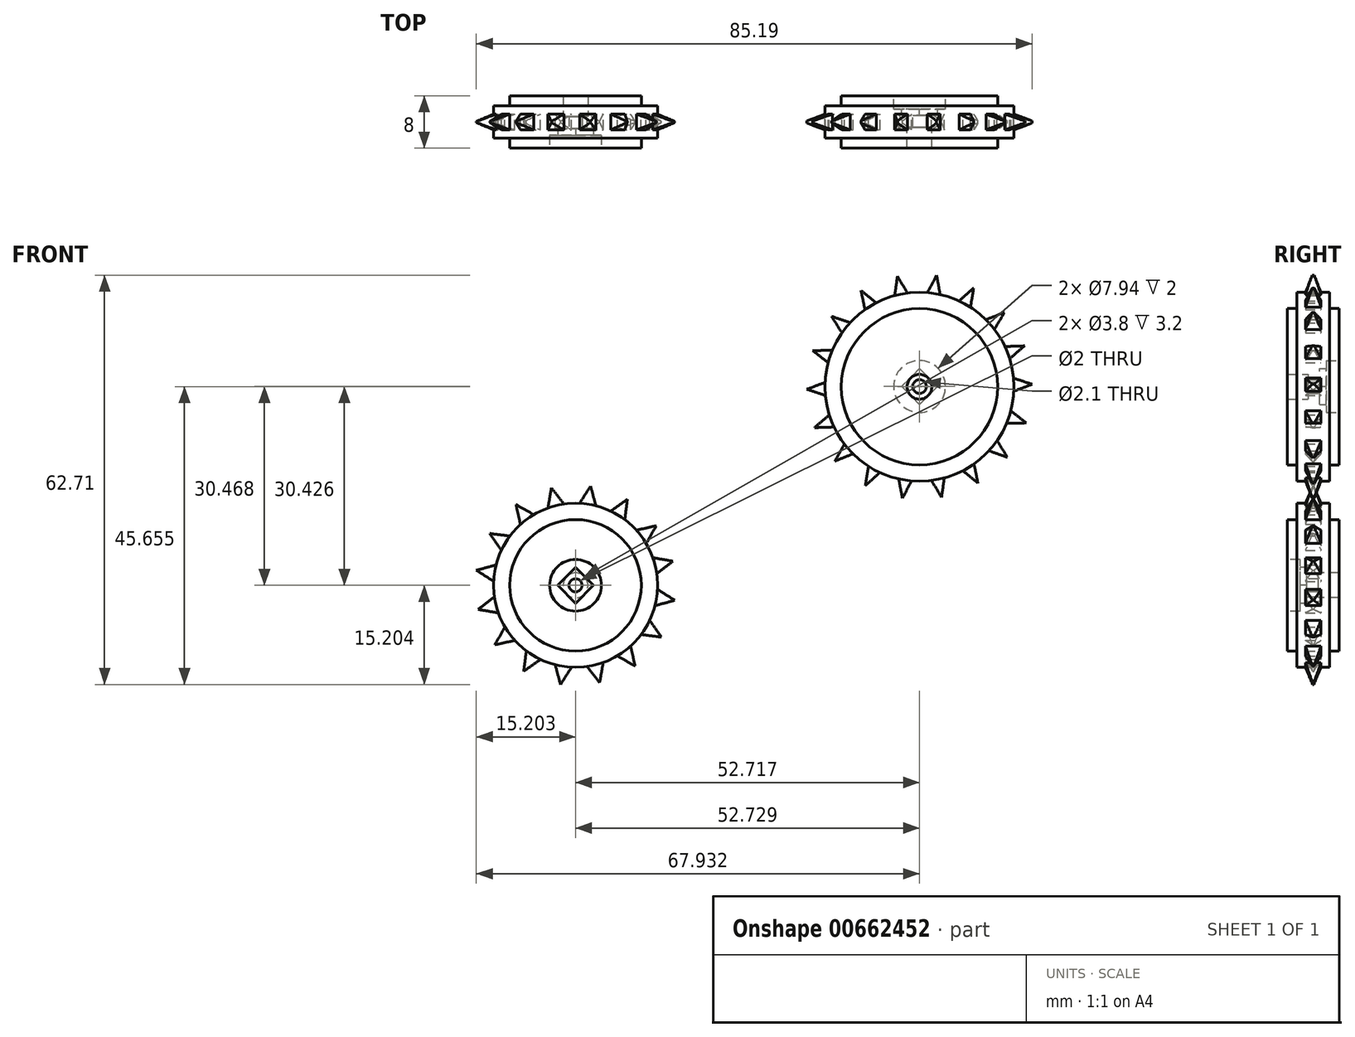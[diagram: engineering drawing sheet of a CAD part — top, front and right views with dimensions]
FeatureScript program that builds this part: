
annotation { "Feature Type Name" : "Feature", "Feature Type Description" : "" }
export const myFeature = defineFeature(function(context is Context, id is Id, definition is map)
    precondition{}
    {
        {
            var Q0;
            Q0=qCreatedBy(makeId("Front.planeOp"),FACE);
            var sketch = newSketch(context, id + "F0", { "sketchPlane" : qUnion([Q0])});
            skCircle(sketch, "E0.cCircle", {"center": v(0, 0) * mm, "radius": 17.01 * mm, "construction": true});
            skLineSegment(sketch, "E0.0", {"start": v(16.36, -5.55) * mm, "end": v(13.48, -10.8) * mm});
            skLineSegment(sketch, "E0.1", {"start": v(13.48, -10.8) * mm, "end": v(8.97, -14.77) * mm});
            skLineSegment(sketch, "E0.2", {"start": v(8.97, -14.77) * mm, "end": v(3.38, -16.94) * mm});
            skLineSegment(sketch, "E0.3", {"start": v(3.38, -16.94) * mm, "end": v(-2.62, -17.08) * mm});
            skLineSegment(sketch, "E0.4", {"start": v(-2.62, -17.08) * mm, "end": v(-8.3, -15.15) * mm});
            skLineSegment(sketch, "E0.5", {"start": v(-8.3, -15.15) * mm, "end": v(-12.98, -11.4) * mm});
            skLineSegment(sketch, "E0.6", {"start": v(-12.98, -11.4) * mm, "end": v(-16.1, -6.27) * mm});
            skLineSegment(sketch, "E0.7", {"start": v(-16.1, -6.27) * mm, "end": v(-17.27, -0.38) * mm});
            skLineSegment(sketch, "E0.8", {"start": v(-17.27, -0.38) * mm, "end": v(-16.36, 5.55) * mm});
            skLineSegment(sketch, "E0.9", {"start": v(-16.36, 5.55) * mm, "end": v(-13.48, 10.8) * mm});
            skLineSegment(sketch, "E0.10", {"start": v(-13.48, 10.8) * mm, "end": v(-8.97, 14.77) * mm});
            skLineSegment(sketch, "E0.11", {"start": v(-8.97, 14.77) * mm, "end": v(-3.38, 16.94) * mm});
            skLineSegment(sketch, "E0.12", {"start": v(-3.38, 16.94) * mm, "end": v(2.62, 17.08) * mm});
            skLineSegment(sketch, "E0.13", {"start": v(2.62, 17.08) * mm, "end": v(8.3, 15.15) * mm});
            skLineSegment(sketch, "E0.14", {"start": v(8.3, 15.15) * mm, "end": v(12.98, 11.4) * mm});
            skLineSegment(sketch, "E0.15", {"start": v(12.98, 11.4) * mm, "end": v(16.1, 6.27) * mm});
            skLineSegment(sketch, "E0.16", {"start": v(16.1, 6.27) * mm, "end": v(17.27, 0.38) * mm});
            skLineSegment(sketch, "E0.17", {"start": v(17.27, 0.38) * mm, "end": v(16.36, -5.55) * mm});
            skPoint(sketch, "E0.0.midPoint", {"position": v(14.92, -8.18) * mm});
            skLineSegment(sketch, "E1", {"start": v(-61.38, -2.75) * mm, "end": v(-43.67, -5.95) * mm});
            skLineSegment(sketch, "E2", {"start": v(-3.38, 16.94) * mm, "end": v(-2.83, 14.2) * mm, "construction": true});
            skLineSegment(sketch, "E3", {"start": v(-2.83, 14.2) * mm, "end": v(-2.34, 11.75) * mm, "construction": true});
            skLineSegment(sketch, "E4", {"start": v(-2.34, 11.75) * mm, "end": v(0, 0) * mm, "construction": true});
            skCircle(sketch, "E5", {"center": v(0, 0) * mm, "radius": 11.98 * mm});
            skCircle(sketch, "E6", {"center": v(0, 0) * mm, "radius": 14.48 * mm});
            skLineSegment(sketch, "E7", {"start": v(0, 0) * mm, "end": v(2.62, 17.08) * mm, "construction": true});
            skPoint(sketch, "E8", {"position": v(2.13, 13.85) * mm});
            skLineSegment(sketch, "E9", {"start": v(2.13, 13.85) * mm, "end": v(0.99, 14.03) * mm, "construction": true});
            skLineSegment(sketch, "E10", {"start": v(2.62, 17.08) * mm, "end": v(0.99, 14.03) * mm});
            skLineSegment(sketch, "E11.MirrorCS", {"start": v(2.62, 17.08) * mm, "end": v(3.26, 13.68) * mm});
            skLineSegment(sketch, "E12.14.0", {"start": v(16.7, 0.37) * mm, "end": v(13.41, 1.45) * mm});
            skPoint(sketch, "E13.0", {"position": v(0.01, 0.03) * mm});
            skCircle(sketch, "E14.cCircle", {"center": v(0.01, 0.03) * mm, "radius": 2.75 * mm, "construction": true});
            skLineSegment(sketch, "E14.0", {"start": v(-2.74, 0.03) * mm, "end": v(0.01, 2.78) * mm});
            skLineSegment(sketch, "E14.1", {"start": v(0.01, 2.78) * mm, "end": v(2.76, 0.03) * mm});
            skLineSegment(sketch, "E14.2", {"start": v(2.76, 0.03) * mm, "end": v(0.01, -2.73) * mm});
            skLineSegment(sketch, "E14.3", {"start": v(0.01, -2.73) * mm, "end": v(-2.74, 0.03) * mm});
            skCircle(sketch, "E15", {"center": v(0.01, 0.03) * mm, "radius": 1.05 * mm});
            skCircle(sketch, "E16", {"center": v(0.01, 0.03) * mm, "radius": 3.97 * mm});
            skLineSegment(sketch, "E17", {"start": v(2.13, 13.85) * mm, "end": v(2.75, 17.9) * mm});
            skLineSegment(sketch, "E18.1.0", {"start": v(-2.74, 13.75) * mm, "end": v(-3.87, 13.52) * mm, "construction": true});
            skPoint(sketch, "E18.1.1", {"position": v(-2.74, 13.75) * mm});
            skLineSegment(sketch, "E18.1.2", {"start": v(-3.38, 16.94) * mm, "end": v(-3.87, 13.52) * mm});
            skLineSegment(sketch, "E18.1.3", {"start": v(-3.38, 16.94) * mm, "end": v(-1.61, 13.97) * mm});
            skLineSegment(sketch, "E18.2.0", {"start": v(-7.28, 11.98) * mm, "end": v(-8.26, 11.38) * mm, "construction": true});
            skPoint(sketch, "E18.2.1", {"position": v(-7.28, 11.98) * mm});
            skLineSegment(sketch, "E18.2.2", {"start": v(-8.97, 14.77) * mm, "end": v(-8.26, 11.38) * mm});
            skLineSegment(sketch, "E18.2.3", {"start": v(-8.97, 14.77) * mm, "end": v(-6.3, 12.58) * mm});
            skLineSegment(sketch, "E18.3.0", {"start": v(-10.94, 8.77) * mm, "end": v(-11.66, 7.87) * mm, "construction": true});
            skPoint(sketch, "E18.3.1", {"position": v(-10.94, 8.77) * mm});
            skLineSegment(sketch, "E18.3.2", {"start": v(-13.48, 10.8) * mm, "end": v(-11.66, 7.87) * mm});
            skLineSegment(sketch, "E18.3.3", {"start": v(-13.48, 10.8) * mm, "end": v(-10.22, 9.67) * mm});
            skLineSegment(sketch, "E18.4.0", {"start": v(-13.28, 4.5) * mm, "end": v(-13.64, 3.41) * mm, "construction": true});
            skPoint(sketch, "E18.4.1", {"position": v(-13.28, 4.5) * mm});
            skLineSegment(sketch, "E18.4.2", {"start": v(-16.36, 5.55) * mm, "end": v(-13.64, 3.41) * mm});
            skLineSegment(sketch, "E18.4.3", {"start": v(-16.36, 5.55) * mm, "end": v(-12.9, 5.59) * mm});
            skLineSegment(sketch, "E18.5.0", {"start": v(-14.01, -0.31) * mm, "end": v(-13.99, -1.46) * mm, "construction": true});
            skPoint(sketch, "E18.5.1", {"position": v(-14.01, -0.31) * mm});
            skLineSegment(sketch, "E18.5.2", {"start": v(-17.27, -0.38) * mm, "end": v(-13.99, -1.46) * mm});
            skLineSegment(sketch, "E18.5.3", {"start": v(-17.27, -0.38) * mm, "end": v(-14.04, 0.84) * mm});
            skLineSegment(sketch, "E18.6.0", {"start": v(-13.06, -5.09) * mm, "end": v(-12.64, -6.16) * mm, "construction": true});
            skPoint(sketch, "E18.6.1", {"position": v(-13.06, -5.09) * mm});
            skLineSegment(sketch, "E18.6.2", {"start": v(-16.1, -6.27) * mm, "end": v(-12.64, -6.16) * mm});
            skLineSegment(sketch, "E18.6.3", {"start": v(-16.1, -6.27) * mm, "end": v(-13.48, -4.01) * mm});
            skLineSegment(sketch, "E18.7.0", {"start": v(-10.53, -9.25) * mm, "end": v(-9.78, -10.11) * mm, "construction": true});
            skPoint(sketch, "E18.7.1", {"position": v(-10.53, -9.25) * mm});
            skLineSegment(sketch, "E18.7.2", {"start": v(-12.98, -11.4) * mm, "end": v(-9.78, -10.11) * mm});
            skLineSegment(sketch, "E18.7.3", {"start": v(-12.98, -11.4) * mm, "end": v(-11.3, -8.38) * mm});
            skLineSegment(sketch, "E18.8.0", {"start": v(-6.74, -12.3) * mm, "end": v(-5.73, -12.84) * mm, "construction": true});
            skPoint(sketch, "E18.8.1", {"position": v(-6.74, -12.3) * mm});
            skLineSegment(sketch, "E18.8.2", {"start": v(-8.3, -15.15) * mm, "end": v(-5.73, -12.84) * mm});
            skLineSegment(sketch, "E18.8.3", {"start": v(-8.3, -15.15) * mm, "end": v(-7.75, -11.74) * mm});
            skLineSegment(sketch, "E18.9.0", {"start": v(-2.13, -13.85) * mm, "end": v(-0.99, -14.03) * mm, "construction": true});
            skPoint(sketch, "E18.9.1", {"position": v(-2.13, -13.85) * mm});
            skLineSegment(sketch, "E18.9.2", {"start": v(-2.62, -17.08) * mm, "end": v(-0.99, -14.03) * mm});
            skLineSegment(sketch, "E18.9.3", {"start": v(-2.62, -17.08) * mm, "end": v(-3.26, -13.68) * mm});
            skLineSegment(sketch, "E18.10.0", {"start": v(2.74, -13.75) * mm, "end": v(3.87, -13.52) * mm, "construction": true});
            skPoint(sketch, "E18.10.1", {"position": v(2.74, -13.75) * mm});
            skLineSegment(sketch, "E18.10.2", {"start": v(3.38, -16.94) * mm, "end": v(3.87, -13.52) * mm});
            skLineSegment(sketch, "E18.10.3", {"start": v(3.38, -16.94) * mm, "end": v(1.61, -13.97) * mm});
            skLineSegment(sketch, "E18.11.0", {"start": v(7.28, -11.98) * mm, "end": v(8.26, -11.38) * mm, "construction": true});
            skPoint(sketch, "E18.11.1", {"position": v(7.28, -11.98) * mm});
            skLineSegment(sketch, "E18.11.2", {"start": v(8.97, -14.77) * mm, "end": v(8.26, -11.38) * mm});
            skLineSegment(sketch, "E18.11.3", {"start": v(8.97, -14.77) * mm, "end": v(6.3, -12.58) * mm});
            skLineSegment(sketch, "E18.12.0", {"start": v(10.94, -8.77) * mm, "end": v(11.66, -7.87) * mm, "construction": true});
            skPoint(sketch, "E18.12.1", {"position": v(10.94, -8.77) * mm});
            skLineSegment(sketch, "E18.12.2", {"start": v(13.48, -10.8) * mm, "end": v(11.66, -7.87) * mm});
            skLineSegment(sketch, "E18.12.3", {"start": v(13.48, -10.8) * mm, "end": v(10.22, -9.67) * mm});
            skLineSegment(sketch, "E18.13.0", {"start": v(13.28, -4.5) * mm, "end": v(13.64, -3.41) * mm, "construction": true});
            skPoint(sketch, "E18.13.1", {"position": v(13.28, -4.5) * mm});
            skLineSegment(sketch, "E18.13.2", {"start": v(16.36, -5.55) * mm, "end": v(13.64, -3.41) * mm});
            skLineSegment(sketch, "E18.13.3", {"start": v(16.36, -5.55) * mm, "end": v(12.9, -5.59) * mm});
            skLineSegment(sketch, "E18.14.0", {"start": v(14.01, 0.31) * mm, "end": v(13.99, 1.46) * mm, "construction": true});
            skPoint(sketch, "E18.14.1", {"position": v(14.01, 0.31) * mm});
            skLineSegment(sketch, "E18.14.2", {"start": v(17.27, 0.38) * mm, "end": v(13.99, 1.46) * mm});
            skLineSegment(sketch, "E18.14.3", {"start": v(17.27, 0.38) * mm, "end": v(14.04, -0.84) * mm});
            skLineSegment(sketch, "E18.15.0", {"start": v(13.06, 5.09) * mm, "end": v(12.64, 6.16) * mm, "construction": true});
            skPoint(sketch, "E18.15.1", {"position": v(13.06, 5.09) * mm});
            skLineSegment(sketch, "E18.15.2", {"start": v(16.1, 6.27) * mm, "end": v(12.64, 6.16) * mm});
            skLineSegment(sketch, "E18.15.3", {"start": v(16.1, 6.27) * mm, "end": v(13.48, 4.01) * mm});
            skLineSegment(sketch, "E18.16.0", {"start": v(10.53, 9.25) * mm, "end": v(9.78, 10.11) * mm, "construction": true});
            skPoint(sketch, "E18.16.1", {"position": v(10.53, 9.25) * mm});
            skLineSegment(sketch, "E18.16.2", {"start": v(12.98, 11.4) * mm, "end": v(9.78, 10.11) * mm});
            skLineSegment(sketch, "E18.16.3", {"start": v(12.98, 11.4) * mm, "end": v(11.3, 8.38) * mm});
            skLineSegment(sketch, "E18.17.0", {"start": v(6.74, 12.3) * mm, "end": v(5.73, 12.84) * mm, "construction": true});
            skPoint(sketch, "E18.17.1", {"position": v(6.74, 12.3) * mm});
            skLineSegment(sketch, "E18.17.2", {"start": v(8.3, 15.15) * mm, "end": v(5.73, 12.84) * mm});
            skLineSegment(sketch, "E18.17.3", {"start": v(8.3, 15.15) * mm, "end": v(7.75, 11.74) * mm});
            skSolve(sketch);
        }
        {
            var Q0;
            Q0=makeQuery(id+"F0.imprint","IMPRINT",FACE,{"disambiguationData":[TD([[makeQuery(id+"F0.imprint","IMPRINT",EDGE,{"derivedFrom":sQuery(id+"F0.wireOp",EDGE,"E5")}),-1.0]])]});
            var Q1;
            {var subQ0=sQuery(id+"F0.wireOp",EDGE,"E12.7.1");var subQ1=sQuery(id+"F0.wireOp",EDGE,"E6");var subQ2=makeQuery(id+"F0.imprint","INTERSECT",VERTEX,{"derivedFrom":[subQ1,subQ0]});Q1=makeQuery(id+"F0.imprint","IMPRINT",FACE,{"disambiguationData":[TD([[makeQuery(id+"F0.imprint","IMPRINT",EDGE,{"disambiguationData":[TD([[subQ2,-1.0]])],"derivedFrom":subQ1}),-1.0]])]});}
            var Q2;
            {var subQ0=sQuery(id+"F0.wireOp",EDGE,"E12.8.1");var subQ1=sQuery(id+"F0.wireOp",EDGE,"E6");var subQ2=makeQuery(id+"F0.imprint","INTERSECT",VERTEX,{"derivedFrom":[subQ1,subQ0]});Q2=makeQuery(id+"F0.imprint","IMPRINT",FACE,{"disambiguationData":[TD([[makeQuery(id+"F0.imprint","IMPRINT",EDGE,{"disambiguationData":[TD([[subQ2,-1.0]])],"derivedFrom":subQ1}),-1.0]])]});}
            var Q3;
            {var subQ0=sQuery(id+"F0.wireOp",EDGE,"E12.9.1");var subQ1=sQuery(id+"F0.wireOp",EDGE,"E6");var subQ2=makeQuery(id+"F0.imprint","INTERSECT",VERTEX,{"derivedFrom":[subQ1,subQ0]});Q3=makeQuery(id+"F0.imprint","IMPRINT",FACE,{"disambiguationData":[TD([[makeQuery(id+"F0.imprint","IMPRINT",EDGE,{"disambiguationData":[TD([[subQ2,-1.0]])],"derivedFrom":subQ1}),-1.0]])]});}
            var Q4;
            {var subQ0=sQuery(id+"F0.wireOp",EDGE,"E12.10.1");var subQ1=sQuery(id+"F0.wireOp",EDGE,"E6");var subQ2=makeQuery(id+"F0.imprint","INTERSECT",VERTEX,{"derivedFrom":[subQ1,subQ0]});Q4=makeQuery(id+"F0.imprint","IMPRINT",FACE,{"disambiguationData":[TD([[makeQuery(id+"F0.imprint","IMPRINT",EDGE,{"disambiguationData":[TD([[subQ2,-1.0]])],"derivedFrom":subQ1}),-1.0]])]});}
            var Q5;
            {var subQ0=sQuery(id+"F0.wireOp",EDGE,"E12.11.1");var subQ1=sQuery(id+"F0.wireOp",EDGE,"E6");var subQ2=makeQuery(id+"F0.imprint","INTERSECT",VERTEX,{"derivedFrom":[subQ1,subQ0]});Q5=makeQuery(id+"F0.imprint","IMPRINT",FACE,{"disambiguationData":[TD([[makeQuery(id+"F0.imprint","IMPRINT",EDGE,{"disambiguationData":[TD([[subQ2,-1.0]])],"derivedFrom":subQ1}),-1.0]])]});}
            var Q6;
            {var subQ0=sQuery(id+"F0.wireOp",EDGE,"E12.12.1");var subQ1=sQuery(id+"F0.wireOp",EDGE,"E6");var subQ2=makeQuery(id+"F0.imprint","INTERSECT",VERTEX,{"derivedFrom":[subQ1,subQ0]});Q6=makeQuery(id+"F0.imprint","IMPRINT",FACE,{"disambiguationData":[TD([[makeQuery(id+"F0.imprint","IMPRINT",EDGE,{"disambiguationData":[TD([[subQ2,-1.0]])],"derivedFrom":subQ1}),-1.0]])]});}
            var Q7;
            {var subQ0=sQuery(id+"F0.wireOp",EDGE,"E12.13.1");var subQ1=sQuery(id+"F0.wireOp",EDGE,"E6");var subQ2=makeQuery(id+"F0.imprint","INTERSECT",VERTEX,{"derivedFrom":[subQ1,subQ0]});Q7=makeQuery(id+"F0.imprint","IMPRINT",FACE,{"disambiguationData":[TD([[makeQuery(id+"F0.imprint","IMPRINT",EDGE,{"disambiguationData":[TD([[subQ2,-1.0]])],"derivedFrom":subQ1}),-1.0]])]});}
            var Q8;
            Q8=makeQuery(id+"F0.imprint","IMPRINT",FACE,{"disambiguationData":[TD([[makeQuery(id+"F0.imprint","IMPRINT",EDGE,{"derivedFrom":sQuery(id+"F0.wireOp",EDGE,"E5")}),1.0]])]});
            var Q9;
            {var subQ0=sQuery(id+"F0.wireOp",EDGE,"E12.14.0");var subQ1=sQuery(id+"F0.wireOp",EDGE,"E6");var subQ2=makeQuery(id+"F0.imprint","INTERSECT",VERTEX,{"derivedFrom":[subQ1,subQ0]});Q9=makeQuery(id+"F0.imprint","IMPRINT",FACE,{"disambiguationData":[TD([[makeQuery(id+"F0.imprint","IMPRINT",EDGE,{"disambiguationData":[TD([[subQ2,1.0]])],"derivedFrom":subQ1}),-1.0]])]});}
            var Q10;
            {var subQ0=sQuery(id+"F0.wireOp",EDGE,"E12.15.1");var subQ1=sQuery(id+"F0.wireOp",EDGE,"E6");var subQ2=makeQuery(id+"F0.imprint","INTERSECT",VERTEX,{"derivedFrom":[subQ1,subQ0]});Q10=makeQuery(id+"F0.imprint","IMPRINT",FACE,{"disambiguationData":[TD([[makeQuery(id+"F0.imprint","IMPRINT",EDGE,{"disambiguationData":[TD([[subQ2,-1.0]])],"derivedFrom":subQ1}),-1.0]])]});}
            var Q11;
            {var subQ0=sQuery(id+"F0.wireOp",EDGE,"E12.16.1");var subQ1=sQuery(id+"F0.wireOp",EDGE,"E6");var subQ2=makeQuery(id+"F0.imprint","INTERSECT",VERTEX,{"derivedFrom":[subQ1,subQ0]});Q11=makeQuery(id+"F0.imprint","IMPRINT",FACE,{"disambiguationData":[TD([[makeQuery(id+"F0.imprint","IMPRINT",EDGE,{"disambiguationData":[TD([[subQ2,-1.0]])],"derivedFrom":subQ1}),-1.0]])]});}
            var Q12;
            {var subQ0=sQuery(id+"F0.wireOp",EDGE,"E12.17.1");var subQ1=sQuery(id+"F0.wireOp",EDGE,"E6");var subQ2=makeQuery(id+"F0.imprint","INTERSECT",VERTEX,{"derivedFrom":[subQ1,subQ0]});Q12=makeQuery(id+"F0.imprint","IMPRINT",FACE,{"disambiguationData":[TD([[makeQuery(id+"F0.imprint","IMPRINT",EDGE,{"disambiguationData":[TD([[subQ2,-1.0]])],"derivedFrom":subQ1}),-1.0]])]});}
            var Q13;
            {var subQ0=sQuery(id+"F0.wireOp",EDGE,"E11.MirrorCS");var subQ1=sQuery(id+"F0.wireOp",EDGE,"E6");var subQ2=makeQuery(id+"F0.imprint","INTERSECT",VERTEX,{"derivedFrom":[subQ1,subQ0]});Q13=makeQuery(id+"F0.imprint","IMPRINT",FACE,{"disambiguationData":[TD([[makeQuery(id+"F0.imprint","IMPRINT",EDGE,{"disambiguationData":[TD([[subQ2,-1.0]])],"derivedFrom":subQ1}),-1.0]])]});}
            var Q14;
            {var subQ0=sQuery(id+"F0.wireOp",EDGE,"E12.1.1");var subQ1=sQuery(id+"F0.wireOp",EDGE,"E6");var subQ2=makeQuery(id+"F0.imprint","INTERSECT",VERTEX,{"derivedFrom":[subQ1,subQ0]});Q14=makeQuery(id+"F0.imprint","IMPRINT",FACE,{"disambiguationData":[TD([[makeQuery(id+"F0.imprint","IMPRINT",EDGE,{"disambiguationData":[TD([[subQ2,-1.0]])],"derivedFrom":subQ1}),-1.0]])]});}
            var Q15;
            {var subQ0=sQuery(id+"F0.wireOp",EDGE,"E12.2.1");var subQ1=sQuery(id+"F0.wireOp",EDGE,"E6");var subQ2=makeQuery(id+"F0.imprint","INTERSECT",VERTEX,{"derivedFrom":[subQ1,subQ0]});Q15=makeQuery(id+"F0.imprint","IMPRINT",FACE,{"disambiguationData":[TD([[makeQuery(id+"F0.imprint","IMPRINT",EDGE,{"disambiguationData":[TD([[subQ2,-1.0]])],"derivedFrom":subQ1}),-1.0]])]});}
            var Q16;
            {var subQ0=sQuery(id+"F0.wireOp",EDGE,"E12.3.1");var subQ1=sQuery(id+"F0.wireOp",EDGE,"E6");var subQ2=makeQuery(id+"F0.imprint","INTERSECT",VERTEX,{"derivedFrom":[subQ1,subQ0]});Q16=makeQuery(id+"F0.imprint","IMPRINT",FACE,{"disambiguationData":[TD([[makeQuery(id+"F0.imprint","IMPRINT",EDGE,{"disambiguationData":[TD([[subQ2,-1.0]])],"derivedFrom":subQ1}),-1.0]])]});}
            var Q17;
            {var subQ0=sQuery(id+"F0.wireOp",EDGE,"E12.4.1");var subQ1=sQuery(id+"F0.wireOp",EDGE,"E6");var subQ2=makeQuery(id+"F0.imprint","INTERSECT",VERTEX,{"derivedFrom":[subQ1,subQ0]});Q17=makeQuery(id+"F0.imprint","IMPRINT",FACE,{"disambiguationData":[TD([[makeQuery(id+"F0.imprint","IMPRINT",EDGE,{"disambiguationData":[TD([[subQ2,-1.0]])],"derivedFrom":subQ1}),-1.0]])]});}
            var Q18;
            {var subQ0=sQuery(id+"F0.wireOp",EDGE,"E12.5.1");var subQ1=sQuery(id+"F0.wireOp",EDGE,"E6");var subQ2=makeQuery(id+"F0.imprint","INTERSECT",VERTEX,{"derivedFrom":[subQ1,subQ0]});Q18=makeQuery(id+"F0.imprint","IMPRINT",FACE,{"disambiguationData":[TD([[makeQuery(id+"F0.imprint","IMPRINT",EDGE,{"disambiguationData":[TD([[subQ2,-1.0]])],"derivedFrom":subQ1}),-1.0]])]});}
            var Q19;
            {var subQ0=sQuery(id+"F0.wireOp",EDGE,"E12.6.1");var subQ1=sQuery(id+"F0.wireOp",EDGE,"E6");var subQ2=makeQuery(id+"F0.imprint","INTERSECT",VERTEX,{"derivedFrom":[subQ1,subQ0]});Q19=makeQuery(id+"F0.imprint","IMPRINT",FACE,{"disambiguationData":[TD([[makeQuery(id+"F0.imprint","IMPRINT",EDGE,{"disambiguationData":[TD([[subQ2,-1.0]])],"derivedFrom":subQ1}),-1.0]])]});}
            var Q20;
            {var subQ0=sQuery(id+"F0.wireOp",EDGE,"E17");var subQ1=sQuery(id+"F0.wireOp",EDGE,"E6");var subQ2=makeQuery(id+"F0.imprint","INTERSECT",VERTEX,{"derivedFrom":[subQ1,subQ0]});Q20=makeQuery(id+"F0.imprint","IMPRINT",FACE,{"disambiguationData":[TD([[makeQuery(id+"F0.imprint","IMPRINT",EDGE,{"disambiguationData":[TD([[subQ2,-1.0]])],"derivedFrom":subQ1}),-1.0]])]});}
            var Q21;
            {var subQ0=sQuery(id+"F0.wireOp",EDGE,"E6");var subQ1=makeQuery(id+"F0.imprint","IMPRINT",VERTEX,{"derivedFrom":subQ0});Q21=makeQuery(id+"F0.imprint","IMPRINT",FACE,{"disambiguationData":[TD([[makeQuery(id+"F0.imprint","IMPRINT",EDGE,{"disambiguationData":[TD([[subQ1,-1.0]])],"derivedFrom":subQ0}),-1.0]])]});}
            extrude(context, id + "F1", {"entities" : qUnion([Q0, Q1, Q2, Q3, Q4, Q5, Q6, Q7, Q8, Q9, Q10, Q11, Q12, Q13, Q14, Q15, Q16, Q17, Q18, Q19, Q20, Q21]), "endBound" : BoundingType.SYMMETRIC, "depth" : 2.4 * mm, "offsetDistance" : 25 * mm});
        }
        {
            var Q0;
            Q0=makeQuery(id+"F0.imprint","IMPRINT",FACE,{"disambiguationData":[TD([[makeQuery(id+"F0.imprint","IMPRINT",EDGE,{"derivedFrom":sQuery(id+"F0.wireOp",EDGE,"E5")}),-1.0]])]});
            extrude(context, id + "F2", {"entities" : qUnion([Q0]), "operationType" : NewBodyOperationType.ADD, "endBound" : BoundingType.SYMMETRIC, "depth" : 5 * mm, "offsetDistance" : 25 * mm});
        }
        {
            var Q0;
            Q0=makeQuery(id+"F0.imprint","IMPRINT",FACE,{"disambiguationData":[TD([[makeQuery(id+"F0.imprint","IMPRINT",EDGE,{"derivedFrom":sQuery(id+"F0.wireOp",EDGE,"E5")}),1.0]])]});
            var Q1;
            Q1=makeQuery(id+"F0.imprint","IMPRINT",FACE,{"disambiguationData":[TD([[makeQuery(id+"F0.imprint","IMPRINT",EDGE,{"derivedFrom":sQuery(id+"F0.wireOp",EDGE,"f1872843-3049-4890-8a67-7aa9caa9baa1.0")}),-1.0]])]});
            var Q2;
            Q2=makeQuery(id+"F0.imprint","IMPRINT",FACE,{"disambiguationData":[TD([[makeQuery(id+"F0.imprint","IMPRINT",EDGE,{"derivedFrom":sQuery(id+"F0.wireOp",EDGE,"E14.0")}),1.0]])]});
            var Q3;
            Q3=makeQuery(id+"F0.imprint","IMPRINT",FACE,{"disambiguationData":[TD([[makeQuery(id+"F0.imprint","IMPRINT",EDGE,{"derivedFrom":sQuery(id+"F0.wireOp",EDGE,"E14.0")}),-1.0]])]});
            extrude(context, id + "F3", {"entities" : qUnion([Q0, Q1, Q2, Q3]), "operationType" : NewBodyOperationType.ADD, "endBound" : BoundingType.SYMMETRIC, "depth" : 8 * mm, "offsetDistance" : 25 * mm});
        }
        {
            var Q0;
            Q0=makeQuery(id+"F3.opExtrude","CAP_FACE",FACE,{"disambiguationData":[OSD([sQuery(id+"F0.wireOp",EDGE,"E5"),sQuery(id+"F0.wireOp",EDGE,"E15")])],"isStart":true});
            var sketch = newSketch(context, id + "F4", { "sketchPlane" : qUnion([Q0])});
            skPoint(sketch, "E19.0", {"position": v(-0.01, 0.04) * mm});
            skCircle(sketch, "E20.cCircle", {"center": v(-0.01, 0.04) * mm, "radius": 2.75 * mm, "construction": true});
            skLineSegment(sketch, "E20.0", {"start": v(-2.76, 0.04) * mm, "end": v(-0.01, 2.8) * mm});
            skLineSegment(sketch, "E20.1", {"start": v(-0.01, 2.8) * mm, "end": v(2.74, 0.04) * mm});
            skLineSegment(sketch, "E20.2", {"start": v(2.74, 0.04) * mm, "end": v(-0.01, -2.71) * mm});
            skLineSegment(sketch, "E20.3", {"start": v(-0.01, -2.71) * mm, "end": v(-2.76, 0.04) * mm});
            skCircle(sketch, "E21", {"center": v(-0.01, 0.04) * mm, "radius": 1 * mm});
            skCircle(sketch, "E22", {"center": v(-0.01, 0.04) * mm, "radius": 3.97 * mm});
            skSolve(sketch);
        }
        {
            var Q0;
            Q0=makeQuery(id+"F4.imprint","IMPRINT",FACE,{"disambiguationData":[TD([[makeQuery(id+"F4.imprint","IMPRINT",EDGE,{"derivedFrom":sQuery(id+"F4.wireOp",EDGE,"E20.0")}),1.0]])]});
            extrude(context, id + "F5", {"entities" : qUnion([Q0]), "operationType" : NewBodyOperationType.REMOVE, "oppositeDirection" : true, "depth" : 2 * mm, "offsetDistance" : 25 * mm});
        }
        {
            var Q0;
            {var subQ0=sQuery(id+"F0.wireOp",EDGE,"E15");Q0=makeQuery(id+"F5.boolean.opBoolean","SPLIT",FACE,{"disambiguationData":[TD([makeQuery(id+"F3.opExtrude","SWEPT_FACE",FACE,{"disambiguationData":[OSD([subQ0])]})])],"derivedFrom":makeQuery(id+"F3.opExtrude","CAP_FACE",FACE,{"disambiguationData":[OSD([sQuery(id+"F0.wireOp",EDGE,"E5"),subQ0])],"isStart":true})});}
            extrude(context, id + "F6", {"entities" : qUnion([Q0]), "operationType" : NewBodyOperationType.REMOVE, "oppositeDirection" : true, "depth" : 3 * mm, "offsetDistance" : 25 * mm});
        }
        {
            var Q0;
            Q0=sQuery(id+"F0.wireOp",EDGE,"E17");
            extrude(context, id + "F7", {"bodyType" : ToolBodyType.SURFACE, "surfaceEntities" : qUnion([Q0]), "endBound" : BoundingType.SYMMETRIC, "depth" : 8 * mm, "offsetDistance" : 25 * mm});
        }
        {
            var Q0;
            Q0=makeQuery(id+"F7.opExtrude","SWEPT_FACE",FACE,{"disambiguationData":[OSD([sQuery(id+"F0.wireOp",EDGE,"E17")])]});
            var sketch = newSketch(context, id + "F8", { "sketchPlane" : qUnion([Q0])});
            skLineSegment(sketch, "E23.0", {"start": v(1.2, 17.28) * mm, "end": v(1.2, 14.44) * mm});
            skLineSegment(sketch, "E23.1", {"start": v(-1.2, 17.28) * mm, "end": v(-1.2, 14.44) * mm});
            skLineSegment(sketch, "E23.2", {"start": v(-1.2, 17.28) * mm, "end": v(0, 17.28) * mm});
            skPoint(sketch, "E23.3", {"position": v(1.2, 14.48) * mm});
            skPoint(sketch, "E23.4", {"position": v(-1.2, 14.48) * mm});
            skPoint(sketch, "E24", {"position": v(0, 17.28) * mm});
            skLineSegment(sketch, "E25", {"start": v(0, 17.28) * mm, "end": v(1.2, 17.28) * mm});
            skPoint(sketch, "E26", {"position": v(0.16, 17.28) * mm});
            skLineSegment(sketch, "E27", {"start": v(0.16, 17.28) * mm, "end": v(1.2, 14.48) * mm});
            skLineSegment(sketch, "E28", {"start": v(0, 17.05) * mm, "end": v(0, 13.55) * mm, "construction": true});
            skLineSegment(sketch, "E29.MirrorCS", {"start": v(-0.16, 17.28) * mm, "end": v(-1.2, 14.48) * mm});
            skPoint(sketch, "E30", {"position": v(0, 0) * mm});
            skLineSegment(sketch, "E31", {"start": v(0, 0) * mm, "end": v(3.84, 0) * mm, "construction": true});
            skSolve(sketch);
        }
        {
            var Q0;
            {var subQ3=sQuery(id+"F8.wireOp",EDGE,"E29.MirrorCS");Q0=makeQuery(id+"F8.imprint","IMPRINT",FACE,{"disambiguationData":[TD([[makeQuery(id+"F8.imprint","IMPRINT",EDGE,{"derivedFrom":subQ3}),-1.0]])]});}
            var Q1;
            {var subQ3=sQuery(id+"F8.wireOp",EDGE,"E27");Q1=makeQuery(id+"F8.imprint","IMPRINT",FACE,{"disambiguationData":[TD([[makeQuery(id+"F8.imprint","IMPRINT",EDGE,{"derivedFrom":subQ3}),1.0]])]});}
            var Q2;
            Q2=sQuery(id+"F8.wireOp",EDGE,"E31");
            revolve(context, id + "F9", {"operationType" : NewBodyOperationType.REMOVE, "entities" : qUnion([Q0, Q1]), "axis" : qUnion([Q2]), "revolveType" : RevolveType.FULL, "oppositeDirection" : true});
        }
        {
            var Q0;
            Q0=makeQuery(id+"F6.boolean.opBoolean","COPY",FACE,{"derivedFrom":makeQuery(id+"F6.opExtrude","CAP_FACE",FACE,{"disambiguationData":[OSD([sQuery(id+"F0.wireOp",EDGE,"E5"),sQuery(id+"F0.wireOp",EDGE,"E15")])],"isStart":false})});
            var sketch = newSketch(context, id + "F10", { "sketchPlane" : qUnion([Q0])});
            skPoint(sketch, "E32.0", {"position": v(0, 0) * mm});
            skCircle(sketch, "E33", {"center": v(0, 0) * mm, "radius": 1.9 * mm});
            skSolve(sketch);
        }
        {
            var Q0;
            Q0=makeQuery(id+"F10.imprint","IMPRINT",FACE,{"disambiguationData":[TD([[makeQuery(id+"F10.imprint","IMPRINT",EDGE,{"derivedFrom":sQuery(id+"F10.wireOp",EDGE,"E33")}),1.0]])]});
            extrude(context, id + "F11", {"entities" : qUnion([Q0]), "operationType" : NewBodyOperationType.REMOVE, "oppositeDirection" : true, "depth" : 6.97 * mm, "offsetDistance" : 25 * mm, "hasSecondDirection" : true, "secondDirectionOppositeDirection" : true, "secondDirectionDepth" : 1.8 * mm});
        }
        {
            var Q0;
            Q0=qCreatedBy(makeId("Front.planeOp"),FACE);
            var sketch = newSketch(context, id + "F12", { "sketchPlane" : qUnion([Q0])});
            skCircle(sketch, "E34.cCircle", {"center": v(-52.72, -30.43) * mm, "radius": 15.08 * mm, "construction": true});
            skLineSegment(sketch, "E34.0", {"start": v(-39.55, -38.37) * mm, "end": v(-43.6, -42.8) * mm});
            skLineSegment(sketch, "E34.1", {"start": v(-43.6, -42.8) * mm, "end": v(-49.02, -45.35) * mm});
            skLineSegment(sketch, "E34.2", {"start": v(-49.02, -45.35) * mm, "end": v(-55.02, -45.63) * mm});
            skLineSegment(sketch, "E34.3", {"start": v(-55.02, -45.63) * mm, "end": v(-60.66, -43.6) * mm});
            skLineSegment(sketch, "E34.4", {"start": v(-60.66, -43.6) * mm, "end": v(-65.1, -39.55) * mm});
            skLineSegment(sketch, "E34.5", {"start": v(-65.1, -39.55) * mm, "end": v(-67.64, -34.12) * mm});
            skLineSegment(sketch, "E34.6", {"start": v(-67.64, -34.12) * mm, "end": v(-67.92, -28.13) * mm});
            skLineSegment(sketch, "E34.7", {"start": v(-67.92, -28.13) * mm, "end": v(-65.88, -22.48) * mm});
            skLineSegment(sketch, "E34.8", {"start": v(-65.88, -22.48) * mm, "end": v(-61.84, -18.05) * mm});
            skLineSegment(sketch, "E34.9", {"start": v(-61.84, -18.05) * mm, "end": v(-56.41, -15.5) * mm});
            skLineSegment(sketch, "E34.10", {"start": v(-56.41, -15.5) * mm, "end": v(-50.42, -15.22) * mm});
            skLineSegment(sketch, "E34.11", {"start": v(-50.42, -15.22) * mm, "end": v(-44.77, -17.26) * mm});
            skLineSegment(sketch, "E34.12", {"start": v(-44.77, -17.26) * mm, "end": v(-40.34, -21.3) * mm});
            skLineSegment(sketch, "E34.13", {"start": v(-40.34, -21.3) * mm, "end": v(-37.79, -26.73) * mm});
            skLineSegment(sketch, "E34.14", {"start": v(-37.79, -26.73) * mm, "end": v(-37.51, -32.73) * mm});
            skLineSegment(sketch, "E34.15", {"start": v(-37.51, -32.73) * mm, "end": v(-39.55, -38.37) * mm});
            skPoint(sketch, "E34.0.midPoint", {"position": v(-41.57, -40.59) * mm});
            skLineSegment(sketch, "E35", {"start": v(-56.41, -15.5) * mm, "end": v(-52.72, -30.43) * mm, "construction": true});
            skPoint(sketch, "E36", {"position": v(-55.74, -18.22) * mm});
            skPoint(sketch, "E37", {"position": v(-55.14, -20.64) * mm});
            skPoint(sketch, "E38", {"position": v(-55.61, -18.72) * mm});
            skCircle(sketch, "E39", {"center": v(-52.72, -30.43) * mm, "radius": 10.08 * mm});
            skCircle(sketch, "E40", {"center": v(-52.72, -30.43) * mm, "radius": 12.58 * mm});
            skLineSegment(sketch, "E41", {"start": v(-55.61, -18.72) * mm, "end": v(-57.04, -19.07) * mm, "construction": true});
            skLineSegment(sketch, "E42", {"start": v(-56.41, -15.5) * mm, "end": v(-57.04, -19.07) * mm});
            skLineSegment(sketch, "E43.MirrorCS", {"start": v(-56.41, -15.5) * mm, "end": v(-54.2, -18.36) * mm});
            skLineSegment(sketch, "E44.1.0", {"start": v(-61.84, -18.05) * mm, "end": v(-61.05, -21.59) * mm});
            skLineSegment(sketch, "E44.1.1", {"start": v(-61.84, -18.05) * mm, "end": v(-58.7, -19.85) * mm});
            skLineSegment(sketch, "E44.2.0", {"start": v(-65.88, -22.48) * mm, "end": v(-63.8, -25.45) * mm});
            skLineSegment(sketch, "E44.2.1", {"start": v(-65.88, -22.48) * mm, "end": v(-62.29, -22.94) * mm});
            skLineSegment(sketch, "E44.3.0", {"start": v(-67.92, -28.13) * mm, "end": v(-64.86, -30.07) * mm});
            skLineSegment(sketch, "E44.3.1", {"start": v(-67.92, -28.13) * mm, "end": v(-64.42, -27.17) * mm});
            skLineSegment(sketch, "E44.4.0", {"start": v(-67.64, -34.12) * mm, "end": v(-64.07, -34.75) * mm});
            skLineSegment(sketch, "E44.4.1", {"start": v(-67.64, -34.12) * mm, "end": v(-64.78, -31.9) * mm});
            skLineSegment(sketch, "E44.5.0", {"start": v(-65.1, -39.55) * mm, "end": v(-61.56, -38.76) * mm});
            skLineSegment(sketch, "E44.5.1", {"start": v(-65.1, -39.55) * mm, "end": v(-63.3, -36.4) * mm});
            skLineSegment(sketch, "E44.6.0", {"start": v(-60.66, -43.6) * mm, "end": v(-57.7, -41.51) * mm});
            skLineSegment(sketch, "E44.6.1", {"start": v(-60.66, -43.6) * mm, "end": v(-60.2, -40) * mm});
            skLineSegment(sketch, "E44.7.0", {"start": v(-55.02, -45.63) * mm, "end": v(-53.07, -42.57) * mm});
            skLineSegment(sketch, "E44.7.1", {"start": v(-55.02, -45.63) * mm, "end": v(-55.97, -42.13) * mm});
            skLineSegment(sketch, "E44.8.0", {"start": v(-49.02, -45.35) * mm, "end": v(-48.4, -41.78) * mm});
            skLineSegment(sketch, "E44.8.1", {"start": v(-49.02, -45.35) * mm, "end": v(-51.24, -42.49) * mm});
            skLineSegment(sketch, "E44.9.0", {"start": v(-43.6, -42.8) * mm, "end": v(-44.38, -39.27) * mm});
            skLineSegment(sketch, "E44.9.1", {"start": v(-43.6, -42.8) * mm, "end": v(-46.74, -41) * mm});
            skLineSegment(sketch, "E44.10.0", {"start": v(-39.55, -38.37) * mm, "end": v(-41.63, -35.4) * mm});
            skLineSegment(sketch, "E44.10.1", {"start": v(-39.55, -38.37) * mm, "end": v(-43.15, -37.91) * mm});
            skLineSegment(sketch, "E44.11.0", {"start": v(-37.51, -32.73) * mm, "end": v(-40.57, -30.78) * mm});
            skLineSegment(sketch, "E44.11.1", {"start": v(-37.51, -32.73) * mm, "end": v(-41, -33.68) * mm});
            skLineSegment(sketch, "E44.12.0", {"start": v(-37.79, -26.73) * mm, "end": v(-41.36, -26.1) * mm});
            skLineSegment(sketch, "E44.12.1", {"start": v(-37.79, -26.73) * mm, "end": v(-40.66, -28.95) * mm});
            skLineSegment(sketch, "E44.13.0", {"start": v(-40.34, -21.3) * mm, "end": v(-43.88, -22.09) * mm});
            skLineSegment(sketch, "E44.13.1", {"start": v(-40.34, -21.3) * mm, "end": v(-42.14, -24.45) * mm});
            skLineSegment(sketch, "E44.14.0", {"start": v(-44.77, -17.26) * mm, "end": v(-47.74, -19.34) * mm});
            skLineSegment(sketch, "E44.14.1", {"start": v(-44.77, -17.26) * mm, "end": v(-45.23, -20.85) * mm});
            skLineSegment(sketch, "E44.15.0", {"start": v(-50.42, -15.22) * mm, "end": v(-52.36, -18.28) * mm});
            skLineSegment(sketch, "E44.15.1", {"start": v(-50.42, -15.22) * mm, "end": v(-49.46, -18.72) * mm});
            skLineSegment(sketch, "E45", {"start": v(-46.93, -20.84) * mm, "end": v(-44.77, -17.26) * mm});
            skSolve(sketch);
        }
        {
            var Q0;
            Q0=makeQuery(id+"F12.imprint","IMPRINT",FACE,{"disambiguationData":[TD([[makeQuery(id+"F12.imprint","IMPRINT",EDGE,{"derivedFrom":sQuery(id+"F12.wireOp",EDGE,"E39")}),-1.0]])]});
            var Q1;
            Q1=makeQuery(id+"F12.imprint","IMPRINT",FACE,{"disambiguationData":[TD([[makeQuery(id+"F12.imprint","IMPRINT",EDGE,{"derivedFrom":sQuery(id+"F12.wireOp",EDGE,"E39")}),1.0]])]});
            var Q2;
            {var subQ0=sQuery(id+"F12.wireOp",EDGE,"E44.2.1");var subQ1=sQuery(id+"F12.wireOp",EDGE,"E40");var subQ2=makeQuery(id+"F12.imprint","INTERSECT",VERTEX,{"derivedFrom":[subQ1,subQ0]});Q2=makeQuery(id+"F12.imprint","IMPRINT",FACE,{"disambiguationData":[TD([[makeQuery(id+"F12.imprint","IMPRINT",EDGE,{"disambiguationData":[TD([[subQ2,-1.0]])],"derivedFrom":subQ1}),-1.0]])]});}
            var Q3;
            {var subQ0=sQuery(id+"F12.wireOp",EDGE,"E44.3.1");var subQ1=sQuery(id+"F12.wireOp",EDGE,"E40");var subQ2=makeQuery(id+"F12.imprint","INTERSECT",VERTEX,{"derivedFrom":[subQ1,subQ0]});Q3=makeQuery(id+"F12.imprint","IMPRINT",FACE,{"disambiguationData":[TD([[makeQuery(id+"F12.imprint","IMPRINT",EDGE,{"disambiguationData":[TD([[subQ2,-1.0]])],"derivedFrom":subQ1}),-1.0]])]});}
            var Q4;
            {var subQ0=sQuery(id+"F12.wireOp",EDGE,"E44.4.1");var subQ1=sQuery(id+"F12.wireOp",EDGE,"E40");var subQ2=makeQuery(id+"F12.imprint","INTERSECT",VERTEX,{"derivedFrom":[subQ1,subQ0]});Q4=makeQuery(id+"F12.imprint","IMPRINT",FACE,{"disambiguationData":[TD([[makeQuery(id+"F12.imprint","IMPRINT",EDGE,{"disambiguationData":[TD([[subQ2,-1.0]])],"derivedFrom":subQ1}),-1.0]])]});}
            var Q5;
            {var subQ0=sQuery(id+"F12.wireOp",EDGE,"E44.5.1");var subQ1=sQuery(id+"F12.wireOp",EDGE,"E40");var subQ2=makeQuery(id+"F12.imprint","INTERSECT",VERTEX,{"derivedFrom":[subQ1,subQ0]});Q5=makeQuery(id+"F12.imprint","IMPRINT",FACE,{"disambiguationData":[TD([[makeQuery(id+"F12.imprint","IMPRINT",EDGE,{"disambiguationData":[TD([[subQ2,-1.0]])],"derivedFrom":subQ1}),-1.0]])]});}
            var Q6;
            {var subQ0=sQuery(id+"F12.wireOp",EDGE,"E44.6.1");var subQ1=sQuery(id+"F12.wireOp",EDGE,"E40");var subQ2=makeQuery(id+"F12.imprint","INTERSECT",VERTEX,{"derivedFrom":[subQ1,subQ0]});Q6=makeQuery(id+"F12.imprint","IMPRINT",FACE,{"disambiguationData":[TD([[makeQuery(id+"F12.imprint","IMPRINT",EDGE,{"disambiguationData":[TD([[subQ2,-1.0]])],"derivedFrom":subQ1}),-1.0]])]});}
            var Q7;
            {var subQ0=sQuery(id+"F12.wireOp",EDGE,"E44.7.1");var subQ1=sQuery(id+"F12.wireOp",EDGE,"E40");var subQ2=makeQuery(id+"F12.imprint","INTERSECT",VERTEX,{"derivedFrom":[subQ1,subQ0]});Q7=makeQuery(id+"F12.imprint","IMPRINT",FACE,{"disambiguationData":[TD([[makeQuery(id+"F12.imprint","IMPRINT",EDGE,{"disambiguationData":[TD([[subQ2,-1.0]])],"derivedFrom":subQ1}),-1.0]])]});}
            var Q8;
            {var subQ0=sQuery(id+"F12.wireOp",EDGE,"E44.8.1");var subQ1=sQuery(id+"F12.wireOp",EDGE,"E40");var subQ2=makeQuery(id+"F12.imprint","INTERSECT",VERTEX,{"derivedFrom":[subQ1,subQ0]});Q8=makeQuery(id+"F12.imprint","IMPRINT",FACE,{"disambiguationData":[TD([[makeQuery(id+"F12.imprint","IMPRINT",EDGE,{"disambiguationData":[TD([[subQ2,-1.0]])],"derivedFrom":subQ1}),-1.0]])]});}
            var Q9;
            {var subQ0=sQuery(id+"F12.wireOp",EDGE,"E44.10.1");var subQ1=sQuery(id+"F12.wireOp",EDGE,"E40");var subQ2=makeQuery(id+"F12.imprint","INTERSECT",VERTEX,{"derivedFrom":[subQ1,subQ0]});Q9=makeQuery(id+"F12.imprint","IMPRINT",FACE,{"disambiguationData":[TD([[makeQuery(id+"F12.imprint","IMPRINT",EDGE,{"disambiguationData":[TD([[subQ2,-1.0]])],"derivedFrom":subQ1}),-1.0]])]});}
            var Q10;
            {var subQ0=sQuery(id+"F12.wireOp",EDGE,"E44.9.1");var subQ1=sQuery(id+"F12.wireOp",EDGE,"E40");var subQ2=makeQuery(id+"F12.imprint","INTERSECT",VERTEX,{"derivedFrom":[subQ1,subQ0]});Q10=makeQuery(id+"F12.imprint","IMPRINT",FACE,{"disambiguationData":[TD([[makeQuery(id+"F12.imprint","IMPRINT",EDGE,{"disambiguationData":[TD([[subQ2,-1.0]])],"derivedFrom":subQ1}),-1.0]])]});}
            var Q11;
            {var subQ0=sQuery(id+"F12.wireOp",EDGE,"E44.11.1");var subQ1=sQuery(id+"F12.wireOp",EDGE,"E40");var subQ2=makeQuery(id+"F12.imprint","INTERSECT",VERTEX,{"derivedFrom":[subQ1,subQ0]});Q11=makeQuery(id+"F12.imprint","IMPRINT",FACE,{"disambiguationData":[TD([[makeQuery(id+"F12.imprint","IMPRINT",EDGE,{"disambiguationData":[TD([[subQ2,-1.0]])],"derivedFrom":subQ1}),-1.0]])]});}
            var Q12;
            {var subQ0=sQuery(id+"F12.wireOp",EDGE,"E44.12.0");var subQ1=sQuery(id+"F12.wireOp",EDGE,"E40");var subQ2=makeQuery(id+"F12.imprint","INTERSECT",VERTEX,{"derivedFrom":[subQ1,subQ0]});Q12=makeQuery(id+"F12.imprint","IMPRINT",FACE,{"disambiguationData":[TD([[makeQuery(id+"F12.imprint","IMPRINT",EDGE,{"disambiguationData":[TD([[subQ2,1.0]])],"derivedFrom":subQ1}),-1.0]])]});}
            var Q13;
            {var subQ0=sQuery(id+"F12.wireOp",EDGE,"E44.13.1");var subQ1=sQuery(id+"F12.wireOp",EDGE,"E40");var subQ2=makeQuery(id+"F12.imprint","INTERSECT",VERTEX,{"derivedFrom":[subQ1,subQ0]});Q13=makeQuery(id+"F12.imprint","IMPRINT",FACE,{"disambiguationData":[TD([[makeQuery(id+"F12.imprint","IMPRINT",EDGE,{"disambiguationData":[TD([[subQ2,-1.0]])],"derivedFrom":subQ1}),-1.0]])]});}
            var Q14;
            {var subQ0=sQuery(id+"F12.wireOp",EDGE,"E44.14.1");var subQ1=sQuery(id+"F12.wireOp",EDGE,"E40");var subQ2=makeQuery(id+"F12.imprint","INTERSECT",VERTEX,{"derivedFrom":[subQ1,subQ0]});Q14=makeQuery(id+"F12.imprint","IMPRINT",FACE,{"disambiguationData":[TD([[makeQuery(id+"F12.imprint","IMPRINT",EDGE,{"disambiguationData":[TD([[subQ2,-1.0]])],"derivedFrom":subQ1}),-1.0]])]});}
            var Q15;
            {var subQ0=sQuery(id+"F12.wireOp",EDGE,"E44.15.1");var subQ1=sQuery(id+"F12.wireOp",EDGE,"E40");var subQ2=makeQuery(id+"F12.imprint","INTERSECT",VERTEX,{"derivedFrom":[subQ1,subQ0]});Q15=makeQuery(id+"F12.imprint","IMPRINT",FACE,{"disambiguationData":[TD([[makeQuery(id+"F12.imprint","IMPRINT",EDGE,{"disambiguationData":[TD([[subQ2,-1.0]])],"derivedFrom":subQ1}),-1.0]])]});}
            var Q16;
            {var subQ0=sQuery(id+"F12.wireOp",EDGE,"E43.MirrorCS");var subQ1=sQuery(id+"F12.wireOp",EDGE,"E40");var subQ2=makeQuery(id+"F12.imprint","INTERSECT",VERTEX,{"derivedFrom":[subQ1,subQ0]});Q16=makeQuery(id+"F12.imprint","IMPRINT",FACE,{"disambiguationData":[TD([[makeQuery(id+"F12.imprint","IMPRINT",EDGE,{"disambiguationData":[TD([[subQ2,-1.0]])],"derivedFrom":subQ1}),-1.0]])]});}
            var Q17;
            {var subQ0=sQuery(id+"F12.wireOp",EDGE,"E44.1.1");var subQ1=sQuery(id+"F12.wireOp",EDGE,"E40");var subQ2=makeQuery(id+"F12.imprint","INTERSECT",VERTEX,{"derivedFrom":[subQ1,subQ0]});Q17=makeQuery(id+"F12.imprint","IMPRINT",FACE,{"disambiguationData":[TD([[makeQuery(id+"F12.imprint","IMPRINT",EDGE,{"disambiguationData":[TD([[subQ2,-1.0]])],"derivedFrom":subQ1}),-1.0]])]});}
            var Q18;
            {var subQ0=sQuery(id+"F12.wireOp",EDGE,"E45");var subQ1=sQuery(id+"F12.wireOp",EDGE,"E40");var subQ2=makeQuery(id+"F12.imprint","INTERSECT",VERTEX,{"derivedFrom":[subQ1,subQ0]});Q18=makeQuery(id+"F12.imprint","IMPRINT",FACE,{"disambiguationData":[TD([[makeQuery(id+"F12.imprint","IMPRINT",EDGE,{"disambiguationData":[TD([[subQ2,-1.0]])],"derivedFrom":subQ1}),-1.0]])]});}
            extrude(context, id + "F13", {"entities" : qUnion([Q0, Q1, Q2, Q3, Q4, Q5, Q6, Q7, Q8, Q9, Q10, Q11, Q12, Q13, Q14, Q15, Q16, Q17, Q18]), "endBound" : BoundingType.SYMMETRIC, "depth" : 2.4 * mm, "offsetDistance" : 25 * mm});
        }
        {
            var Q0;
            Q0=makeQuery(id+"F12.imprint","IMPRINT",FACE,{"disambiguationData":[TD([[makeQuery(id+"F12.imprint","IMPRINT",EDGE,{"derivedFrom":sQuery(id+"F12.wireOp",EDGE,"E39")}),-1.0]])]});
            var Q1;
            Q1=makeQuery(id+"F12.imprint","IMPRINT",FACE,{"disambiguationData":[TD([[makeQuery(id+"F12.imprint","IMPRINT",EDGE,{"derivedFrom":sQuery(id+"F12.wireOp",EDGE,"E39")}),1.0]])]});
            extrude(context, id + "F14", {"entities" : qUnion([Q0, Q1]), "operationType" : NewBodyOperationType.ADD, "endBound" : BoundingType.SYMMETRIC, "depth" : 5 * mm, "offsetDistance" : 25 * mm});
        }
        {
            var Q0;
            Q0=makeQuery(id+"F12.imprint","IMPRINT",FACE,{"disambiguationData":[TD([[makeQuery(id+"F12.imprint","IMPRINT",EDGE,{"derivedFrom":sQuery(id+"F12.wireOp",EDGE,"E39")}),1.0]])]});
            extrude(context, id + "F15", {"entities" : qUnion([Q0]), "operationType" : NewBodyOperationType.ADD, "endBound" : BoundingType.SYMMETRIC, "depth" : 8 * mm, "offsetDistance" : 25 * mm});
        }
        {
            var Q0;
            Q0=makeQuery(id+"F15.opExtrude","CAP_FACE",FACE,{"disambiguationData":[OSD([sQuery(id+"F12.wireOp",EDGE,"E39")])],"isStart":false});
            var sketch = newSketch(context, id + "F16", { "sketchPlane" : qUnion([Q0])});
            skPoint(sketch, "E46.0", {"position": v(-52.72, -30.43) * mm});
            skCircle(sketch, "E47.cCircle", {"center": v(-52.72, -30.43) * mm, "radius": 2.75 * mm, "construction": true});
            skLineSegment(sketch, "E47.0", {"start": v(-55.47, -30.43) * mm, "end": v(-52.72, -27.67) * mm});
            skLineSegment(sketch, "E47.1", {"start": v(-52.72, -27.67) * mm, "end": v(-49.97, -30.43) * mm});
            skLineSegment(sketch, "E47.2", {"start": v(-49.97, -30.43) * mm, "end": v(-52.72, -33.18) * mm});
            skLineSegment(sketch, "E47.3", {"start": v(-52.72, -33.18) * mm, "end": v(-55.47, -30.43) * mm});
            skCircle(sketch, "E48", {"center": v(-52.72, -30.43) * mm, "radius": 1 * mm});
            skCircle(sketch, "E49", {"center": v(-52.72, -30.43) * mm, "radius": 3.97 * mm});
            skSolve(sketch);
        }
        {
            var Q0;
            Q0=makeQuery(id+"F16.imprint","IMPRINT",FACE,{"disambiguationData":[TD([[makeQuery(id+"F16.imprint","IMPRINT",EDGE,{"derivedFrom":sQuery(id+"F16.wireOp",EDGE,"E48")}),1.0]])]});
            extrude(context, id + "F17", {"entities" : qUnion([Q0]), "operationType" : NewBodyOperationType.REMOVE, "endBound" : BoundingType.THROUGH_ALL, "oppositeDirection" : true, "depth" : 25 * mm, "offsetDistance" : 25 * mm});
        }
        {
            var Q0;
            Q0=makeQuery(id+"F16.imprint","IMPRINT",FACE,{"disambiguationData":[TD([[makeQuery(id+"F16.imprint","IMPRINT",EDGE,{"derivedFrom":sQuery(id+"F16.wireOp",EDGE,"E47.0")}),-1.0]])]});
            extrude(context, id + "F18", {"entities" : qUnion([Q0]), "operationType" : NewBodyOperationType.REMOVE, "oppositeDirection" : true, "depth" : 3 * mm, "offsetDistance" : 25 * mm});
        }
        {
            var Q0;
            Q0=makeQuery(id+"F16.imprint","IMPRINT",FACE,{"disambiguationData":[TD([[makeQuery(id+"F16.imprint","IMPRINT",EDGE,{"derivedFrom":sQuery(id+"F16.wireOp",EDGE,"E47.0")}),1.0]])]});
            extrude(context, id + "F19", {"entities" : qUnion([Q0]), "operationType" : NewBodyOperationType.REMOVE, "oppositeDirection" : true, "depth" : 2 * mm, "offsetDistance" : 25 * mm});
        }
        {
            var Q0;
            Q0=makeQuery(id+"F18.boolean.opBoolean","COPY",FACE,{"derivedFrom":makeQuery(id+"F18.opExtrude","CAP_FACE",FACE,{"disambiguationData":[OSD([sQuery(id+"F16.wireOp",EDGE,"E47.0"),sQuery(id+"F16.wireOp",EDGE,"E47.1"),sQuery(id+"F16.wireOp",EDGE,"E47.2"),sQuery(id+"F16.wireOp",EDGE,"E47.3"),sQuery(id+"F16.wireOp",EDGE,"E48")])],"isStart":false})});
            var sketch = newSketch(context, id + "F20", { "sketchPlane" : qUnion([Q0])});
            skPoint(sketch, "E50.0", {"position": v(-52.72, -30.43) * mm});
            skCircle(sketch, "E51", {"center": v(-52.72, -30.43) * mm, "radius": 1.9 * mm});
            skSolve(sketch);
        }
        {
            var Q0;
            Q0=makeQuery(id+"F20.imprint","IMPRINT",FACE,{"disambiguationData":[TD([[makeQuery(id+"F20.imprint","IMPRINT",EDGE,{"derivedFrom":sQuery(id+"F20.wireOp",EDGE,"E51")}),1.0]])]});
            extrude(context, id + "F21", {"entities" : qUnion([Q0]), "operationType" : NewBodyOperationType.REMOVE, "oppositeDirection" : true, "depth" : 25 * mm, "offsetDistance" : 25 * mm, "hasSecondDirection" : true, "secondDirectionOppositeDirection" : true, "secondDirectionDepth" : 1.8 * mm});
        }
        {
            var Q0;
            Q0=sQuery(id+"F12.wireOp",EDGE,"E45");
            extrude(context, id + "F22", {"bodyType" : ToolBodyType.SURFACE, "surfaceEntities" : qUnion([Q0]), "endBound" : BoundingType.SYMMETRIC, "depth" : 10 * mm, "offsetDistance" : 25 * mm});
        }
        {
            var Q0;
            Q0=makeQuery(id+"F22.opExtrude","SWEPT_FACE",FACE,{"disambiguationData":[OSD([sQuery(id+"F12.wireOp",EDGE,"E45")])]});
            var sketch = newSketch(context, id + "F23", { "sketchPlane" : qUnion([Q0])});
            skLineSegment(sketch, "E52.0", {"start": v(-1.2, -40.7) * mm, "end": v(-1.2, -37.9) * mm});
            skLineSegment(sketch, "E52.1", {"start": v(1.2, -40.7) * mm, "end": v(1.2, -37.9) * mm});
            skLineSegment(sketch, "E53", {"start": v(0, -41.22) * mm, "end": v(0, -37.15) * mm, "construction": true});
            skLineSegment(sketch, "E54", {"start": v(-0.09, -37.9) * mm, "end": v(-1.2, -40.7) * mm});
            skLineSegment(sketch, "E55.MirrorCS", {"start": v(0.09, -37.9) * mm, "end": v(1.2, -40.7) * mm});
            skPoint(sketch, "E56.0", {"position": v(0, -53.28) * mm});
            skLineSegment(sketch, "E57", {"start": v(-7.02, -53.28) * mm, "end": v(6.44, -53.28) * mm, "construction": true});
            skSolve(sketch);
        }
        {
            var Q0;
            {var subQ0=sQuery(id+"F23.wireOp",EDGE,"E52.0");Q0=makeQuery(id+"F23.imprint","IMPRINT",FACE,{"disambiguationData":[TD([[makeQuery(id+"F23.imprint","IMPRINT",EDGE,{"derivedFrom":subQ0}),-1.0]])]});}
            var Q1;
            {var subQ0=sQuery(id+"F23.wireOp",EDGE,"E52.1");Q1=makeQuery(id+"F23.imprint","IMPRINT",FACE,{"disambiguationData":[TD([[makeQuery(id+"F23.imprint","IMPRINT",EDGE,{"derivedFrom":subQ0}),1.0]])]});}
            var Q2;
            Q2=sQuery(id+"F23.wireOp",EDGE,"E57");
            revolve(context, id + "F24", {"operationType" : NewBodyOperationType.REMOVE, "entities" : qUnion([Q0, Q1]), "axis" : qUnion([Q2]), "revolveType" : RevolveType.FULL, "oppositeDirection" : true});
        }
    });
